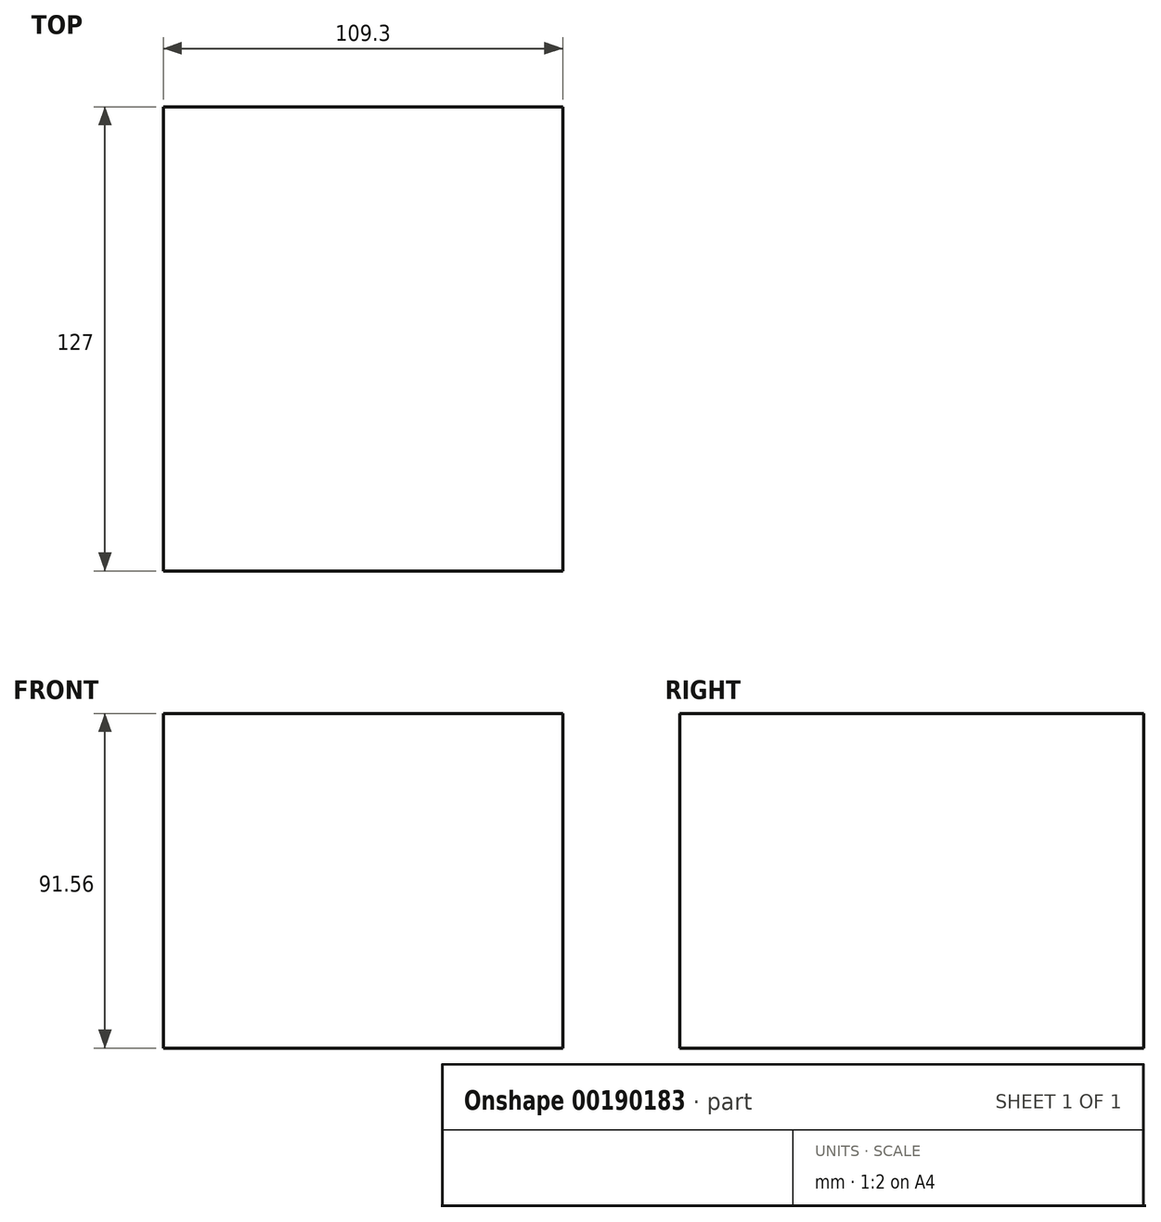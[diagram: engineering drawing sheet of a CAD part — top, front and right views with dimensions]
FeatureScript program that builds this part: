
annotation { "Feature Type Name" : "Feature", "Feature Type Description" : "" }
export const myFeature = defineFeature(function(context is Context, id is Id, definition is map)
    precondition{}
    {
        {
            var Q0;
            Q0=qCreatedBy(makeId("Front.planeOp"),FACE);
            var sketch = newSketch(context, id + "F0", { "sketchPlane" : qUnion([Q0])});
            skLineSegment(sketch, "E0.bottom", {"start": v(54.65, 45.78) * mm, "end": v(-54.65, 45.78) * mm});
            skLineSegment(sketch, "E0.top", {"start": v(54.65, -45.78) * mm, "end": v(-54.65, -45.78) * mm});
            skLineSegment(sketch, "E0.left", {"start": v(54.65, 45.78) * mm, "end": v(54.65, -45.78) * mm});
            skLineSegment(sketch, "E0.right", {"start": v(-54.65, 45.78) * mm, "end": v(-54.65, -45.78) * mm});
            skPoint(sketch, "E0.middle", {"position": v(0, 0) * mm});
            skSolve(sketch);
        }
        {
            var Q0;
            Q0=makeQuery(id+"F0.imprint","IMPRINT",FACE,{"disambiguationData":[TD([[makeQuery(id+"F0.imprint","IMPRINT",EDGE,{"derivedFrom":sQuery(id+"F0.wireOp",EDGE,"E0.bottom")}),1.0]])]});
            extrude(context, id + "F1", {"entities" : qUnion([Q0]), "depth" : 127 * mm});
        }
    });
